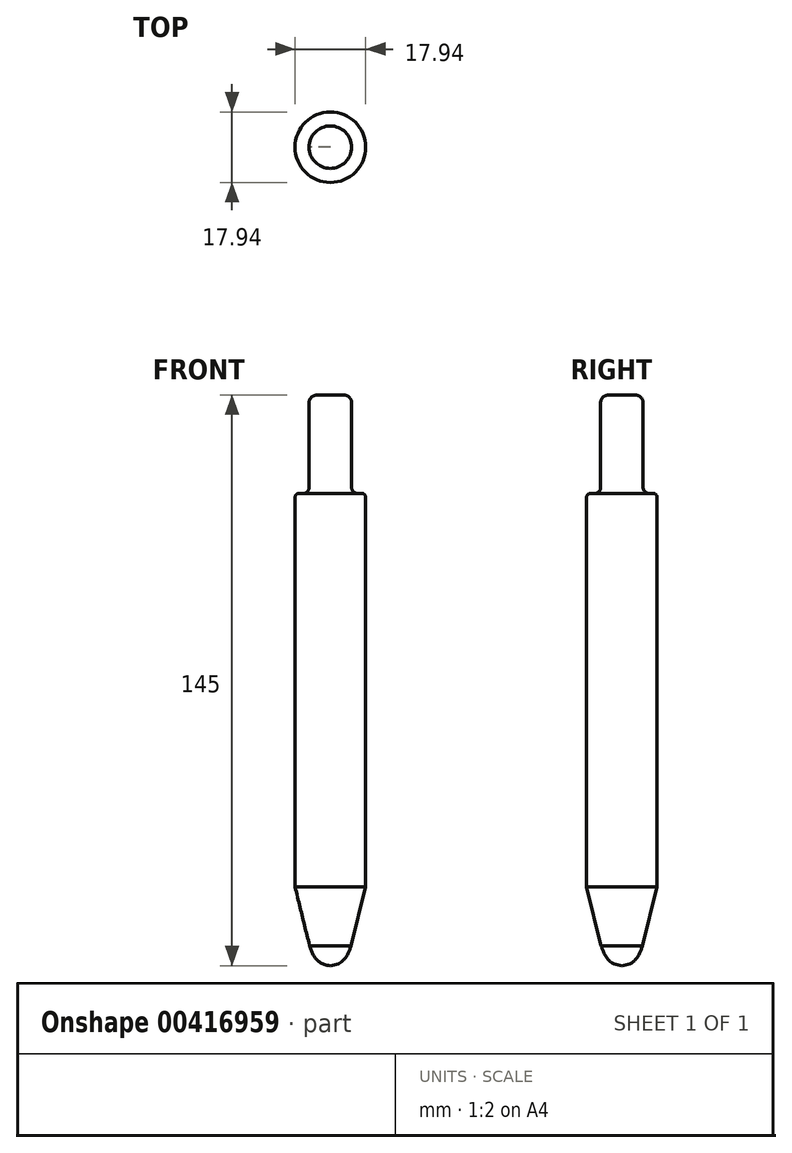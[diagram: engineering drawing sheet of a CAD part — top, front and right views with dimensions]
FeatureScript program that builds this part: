
annotation { "Feature Type Name" : "Feature", "Feature Type Description" : "" }
export const myFeature = defineFeature(function(context is Context, id is Id, definition is map)
    precondition{}
    {
        {
            var Q0;
            Q0=qCreatedBy(makeId("Front.planeOp"),FACE);
            var sketch = newSketch(context, id + "F0", { "sketchPlane" : qUnion([Q0])});
            skLineSegment(sketch, "E0.bottom", {"start": v(0, -53.28) * mm, "end": v(-8.97, -53.28) * mm});
            skLineSegment(sketch, "E0.top", {"start": v(-6.9, 46.72) * mm, "end": v(-7.97, 46.72) * mm});
            skLineSegment(sketch, "E0.left", {"start": v(0, -53.28) * mm, "end": v(0, 46.72) * mm});
            skLineSegment(sketch, "E0.right", {"start": v(-8.97, -53.28) * mm, "end": v(-8.97, 45.72) * mm});
            skLineSegment(sketch, "E1.bottom", {"start": v(-5.4, 46.72) * mm, "end": v(0, 46.72) * mm});
            skLineSegment(sketch, "E1.top", {"start": v(-3.4, 71.72) * mm, "end": v(0, 71.72) * mm});
            skLineSegment(sketch, "E1.left", {"start": v(-5.4, 48.22) * mm, "end": v(-5.4, 69.72) * mm});
            skLineSegment(sketch, "E1.right", {"start": v(0, 46.72) * mm, "end": v(0, 71.72) * mm});
            skLineSegment(sketch, "E2", {"start": v(-8.97, -53.28) * mm, "end": v(-5.29, -68.18) * mm});
            skFitSpline(sketch, "E3", {"points": [v(0, -73.28) * mm, v(-5.29, -68.18) * mm], "startDerivative": vector(-10.08, 1.04) * mm, "endDerivative": vector(-2.87, 8.3) * mm});
            skLineSegment(sketch, "E4", {"start": v(0, -53.28) * mm, "end": v(0, -73.28) * mm});
            skPoint(sketch, "E5.visualSharp", {"position": v(-5.4, 71.72) * mm});
            skArc(sketch, "E5.filletArc", {"start": v(-3.4, 71.72) * mm, "mid": v(-4.81, 71.14) * mm, "end": v(-5.4, 69.72) * mm});
            skPoint(sketch, "E6.visualSharp", {"position": v(-8.97, 46.72) * mm});
            skArc(sketch, "E6.filletArc", {"start": v(-7.97, 46.72) * mm, "mid": v(-8.68, 46.43) * mm, "end": v(-8.97, 45.72) * mm});
            skPoint(sketch, "E7.newPointB", {"position": v(-5.4, 46.72) * mm});
            skArc(sketch, "E7.filletArc", {"start": v(-6.9, 46.72) * mm, "mid": v(-5.84, 47.16) * mm, "end": v(-5.4, 48.22) * mm});
            skSolve(sketch);
        }
        {
            var Q0;
            Q0=makeQuery(id+"F0.imprint","IMPRINT",FACE,{"disambiguationData":[TD([[makeQuery(id+"F0.imprint","IMPRINT",EDGE,{"derivedFrom":sQuery(id+"F0.wireOp",EDGE,"E1.bottom")}),1.0]])]});
            var Q1;
            Q1=makeQuery(id+"F0.imprint","IMPRINT",FACE,{"disambiguationData":[TD([[makeQuery(id+"F0.imprint","IMPRINT",EDGE,{"derivedFrom":sQuery(id+"F0.wireOp",EDGE,"E0.bottom")}),1.0]])]});
            var Q2;
            Q2=makeQuery(id+"F0.imprint","IMPRINT",FACE,{"disambiguationData":[TD([[makeQuery(id+"F0.imprint","IMPRINT",EDGE,{"derivedFrom":sQuery(id+"F0.wireOp",EDGE,"E0.bottom")}),-1.0]])]});
            var Q3;
            Q3=sQuery(id+"F0.wireOp",EDGE,"E0.left");
            revolve(context, id + "F1", {"entities" : qUnion([Q0, Q1, Q2]), "axis" : qUnion([Q3]), "revolveType" : RevolveType.FULL});
        }
    });
